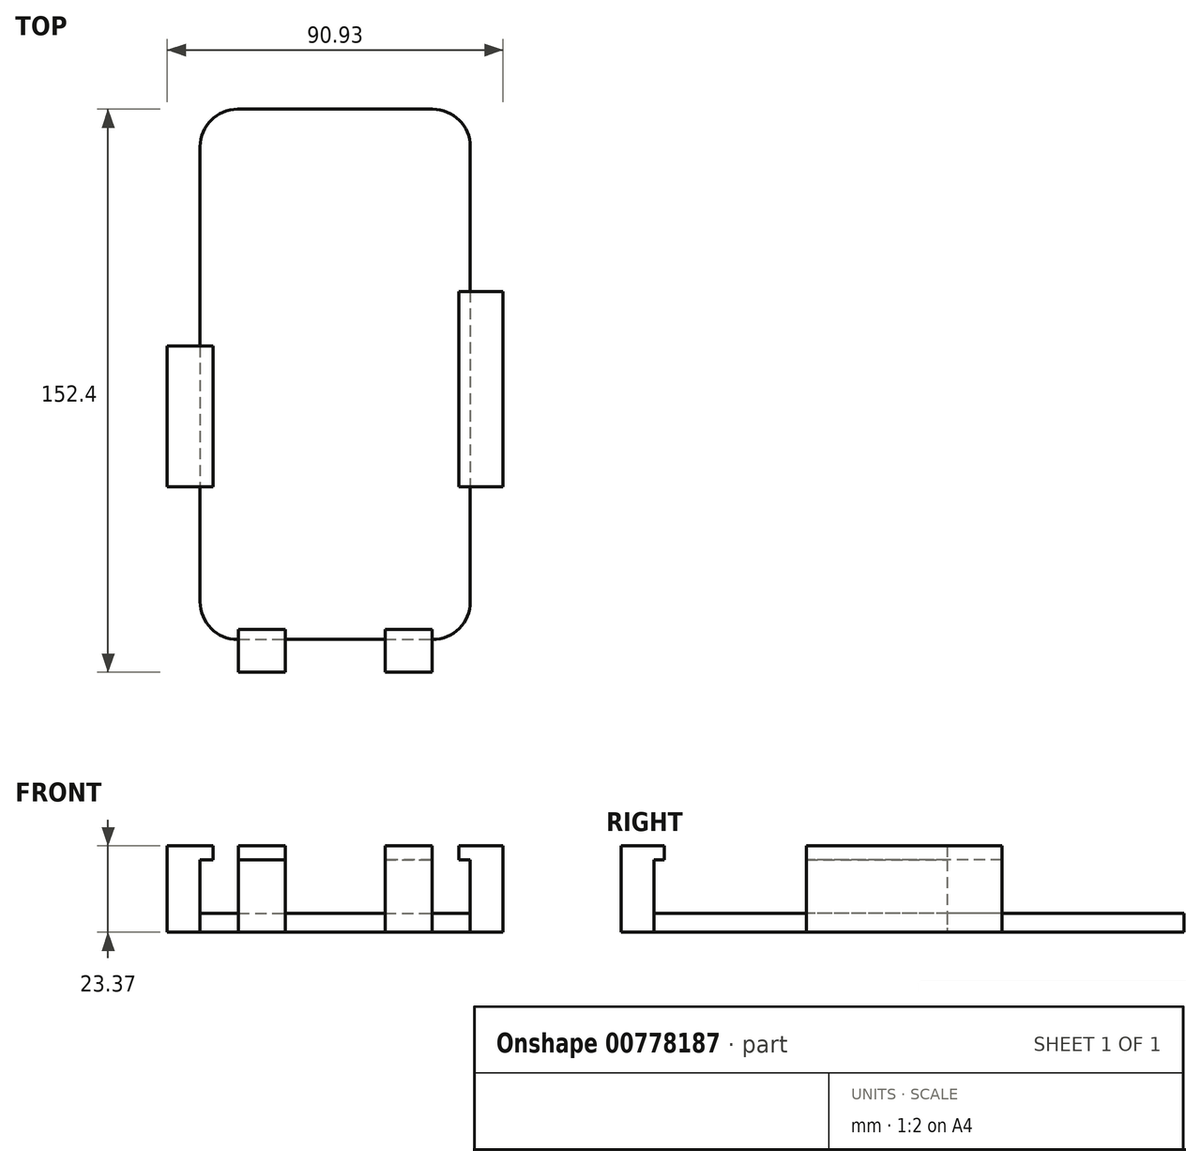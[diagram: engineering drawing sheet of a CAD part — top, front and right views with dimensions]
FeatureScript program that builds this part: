
annotation { "Feature Type Name" : "Feature", "Feature Type Description" : "" }
export const myFeature = defineFeature(function(context is Context, id is Id, definition is map)
    precondition{}
    {
        {
            var Q0;
            Q0=qCreatedBy(makeId("Top.planeOp"),FACE);
            var sketch = newSketch(context, id + "F0", { "sketchPlane" : qUnion([Q0])});
            skLineSegment(sketch, "E0.bottom", {"start": v(-57.8, 102.23) * mm, "end": v(15.34, 102.23) * mm});
            skLineSegment(sketch, "E0.left", {"start": v(-57.8, 102.23) * mm, "end": v(-57.8, -41.28) * mm});
            skLineSegment(sketch, "E0.right", {"start": v(15.34, 102.23) * mm, "end": v(15.34, -41.28) * mm});
            skLineSegment(sketch, "E1", {"start": v(-57.8, 38.1) * mm, "end": v(-66.7, 38.1) * mm});
            skLineSegment(sketch, "E2", {"start": v(-66.7, 38.1) * mm, "end": v(-66.7, 0) * mm});
            skLineSegment(sketch, "E3", {"start": v(-66.7, 0) * mm, "end": v(-57.8, 0) * mm});
            skLineSegment(sketch, "E4", {"start": v(15.34, 52.92) * mm, "end": v(24.23, 52.92) * mm});
            skLineSegment(sketch, "E5", {"start": v(24.23, 52.92) * mm, "end": v(24.23, 0) * mm});
            skLineSegment(sketch, "E6", {"start": v(24.23, 0) * mm, "end": v(15.34, 0) * mm});
            skLineSegment(sketch, "E7", {"start": v(-47.45, -41.28) * mm, "end": v(-47.45, -50.17) * mm});
            skLineSegment(sketch, "E8", {"start": v(-47.45, -50.17) * mm, "end": v(-34.75, -50.17) * mm});
            skLineSegment(sketch, "E9", {"start": v(-34.75, -50.17) * mm, "end": v(-34.75, -41.28) * mm});
            skLineSegment(sketch, "E10", {"start": v(4.98, -41.28) * mm, "end": v(4.98, -50.17) * mm});
            skLineSegment(sketch, "E11", {"start": v(4.98, -50.17) * mm, "end": v(-7.72, -50.17) * mm});
            skLineSegment(sketch, "E12", {"start": v(-7.72, -50.17) * mm, "end": v(-7.72, -41.28) * mm});
            skLineSegment(sketch, "E13", {"start": v(-57.8, -41.28) * mm, "end": v(15.34, -41.28) * mm});
            skSolve(sketch);
        }
        {
            var Q0;
            Q0=makeQuery(id+"F0.imprint","IMPRINT",FACE,{"disambiguationData":[TD([[makeQuery(id+"F0.imprint","IMPRINT",EDGE,{"derivedFrom":sQuery(id+"F0.wireOp",EDGE,"E0.bottom")}),-1.0]])]});
            extrude(context, id + "F1", {"entities" : qUnion([Q0]), "depth" : 5.08 * mm, "offsetDistance" : 25.4 * mm});
        }
        {
            var Q0;
            {var subQ0=sQuery(id+"F0.wireOp",EDGE,"E1");Q0=makeQuery(id+"F0.imprint","IMPRINT",FACE,{"disambiguationData":[TD([[makeQuery(id+"F0.imprint","IMPRINT",EDGE,{"derivedFrom":subQ0}),1.0]])]});}
            var Q1;
            {var subQ0=sQuery(id+"F0.wireOp",EDGE,"E4");Q1=makeQuery(id+"F0.imprint","IMPRINT",FACE,{"disambiguationData":[TD([[makeQuery(id+"F0.imprint","IMPRINT",EDGE,{"derivedFrom":subQ0}),-1.0]])]});}
            var Q2;
            {var subQ0=sQuery(id+"F0.wireOp",EDGE,"E10");Q2=makeQuery(id+"F0.imprint","IMPRINT",FACE,{"disambiguationData":[TD([[makeQuery(id+"F0.imprint","IMPRINT",EDGE,{"derivedFrom":subQ0}),-1.0]])]});}
            var Q3;
            {var subQ0=sQuery(id+"F0.wireOp",EDGE,"E7");Q3=makeQuery(id+"F0.imprint","IMPRINT",FACE,{"disambiguationData":[TD([[makeQuery(id+"F0.imprint","IMPRINT",EDGE,{"derivedFrom":subQ0}),1.0]])]});}
            extrude(context, id + "F2", {"entities" : qUnion([Q0, Q1, Q2, Q3]), "operationType" : NewBodyOperationType.ADD, "depth" : 19.56 * mm, "offsetDistance" : 25.4 * mm});
        }
        {
            var Q0;
            Q0=qCreatedBy(makeId("Top.planeOp"),FACE);
            cPlane(context, id + "F3", {"entities" : qUnion([Q0]), "cplaneType" : CPlaneType.OFFSET, "offset" : 19.56 * mm, "width" : 152.4 * mm, "height" : 152.4 * mm});
        }
        {
            var Q0;
            Q0=qCreatedBy(id+"F3.planeOp",FACE);
            var sketch = newSketch(context, id + "F4", { "sketchPlane" : qUnion([Q0])});
            skLineSegment(sketch, "E14", {"start": v(-66.7, 0) * mm, "end": v(-54.3, 0) * mm});
            skLineSegment(sketch, "E15", {"start": v(-54.3, 0) * mm, "end": v(-54.3, 38.1) * mm});
            skLineSegment(sketch, "E16", {"start": v(-54.3, 38.1) * mm, "end": v(-66.7, 38.1) * mm});
            skLineSegment(sketch, "E17", {"start": v(-66.7, 38.1) * mm, "end": v(-66.7, 0) * mm});
            skLineSegment(sketch, "E18", {"start": v(12.26, 0) * mm, "end": v(24.23, 0) * mm});
            skLineSegment(sketch, "E19", {"start": v(24.23, 0) * mm, "end": v(24.23, 52.92) * mm});
            skLineSegment(sketch, "E20", {"start": v(24.23, 52.92) * mm, "end": v(12.26, 52.92) * mm});
            skLineSegment(sketch, "E21", {"start": v(12.26, 52.92) * mm, "end": v(12.26, 0) * mm});
            skLineSegment(sketch, "E22", {"start": v(-47.44, -38.56) * mm, "end": v(-34.76, -38.56) * mm});
            skLineSegment(sketch, "E23", {"start": v(-34.76, -38.56) * mm, "end": v(-34.76, -50.16) * mm});
            skLineSegment(sketch, "E24", {"start": v(-34.76, -50.16) * mm, "end": v(-47.44, -50.16) * mm});
            skLineSegment(sketch, "E25", {"start": v(-47.44, -50.16) * mm, "end": v(-47.44, -38.56) * mm});
            skLineSegment(sketch, "E26", {"start": v(-7.72, -38.56) * mm, "end": v(-7.72, -50.17) * mm});
            skLineSegment(sketch, "E27", {"start": v(-7.72, -50.17) * mm, "end": v(4.99, -50.17) * mm});
            skLineSegment(sketch, "E28", {"start": v(4.99, -50.17) * mm, "end": v(4.99, -38.56) * mm});
            skLineSegment(sketch, "E29", {"start": v(4.99, -38.56) * mm, "end": v(-7.72, -38.56) * mm});
            skSolve(sketch);
        }
        {
            var Q0;
            Q0 = qSketchRegion(id + "F4", true);
            extrude(context, id + "F5", {"entities" : qUnion([Q0]), "operationType" : NewBodyOperationType.ADD, "depth" : 3.8 * mm, "offsetDistance" : 25.4 * mm});
        }
        {
            var Q0;
            Q0=makeQuery(id+"F1.opExtrude","SWEPT_EDGE",EDGE,{"disambiguationData":[OSD([sQuery(id+"F0.wireOp",EDGE,"E0.left"),sQuery(id+"F0.wireOp",EDGE,"E13")])]});
            var Q1;
            Q1=makeQuery(id+"F1.opExtrude","SWEPT_EDGE",EDGE,{"disambiguationData":[OSD([sQuery(id+"F0.wireOp",EDGE,"E0.right"),sQuery(id+"F0.wireOp",EDGE,"E13")])]});
            var Q2;
            Q2=makeQuery(id+"F1.opExtrude","SWEPT_EDGE",EDGE,{"disambiguationData":[OSD([sQuery(id+"F0.wireOp",EDGE,"E0.bottom"),sQuery(id+"F0.wireOp",EDGE,"E0.right")])]});
            var Q3;
            Q3=makeQuery(id+"F1.opExtrude","SWEPT_EDGE",EDGE,{"disambiguationData":[OSD([sQuery(id+"F0.wireOp",EDGE,"E0.bottom"),sQuery(id+"F0.wireOp",EDGE,"E0.left")])]});
            fillet(context, id + "F6", {"entities" : qUnion([Q0, Q1, Q2, Q3]), "radius" : 10.16 * mm, "tangentPropagation" : true, "allowEdgeOverflow" : false});
        }
    });
